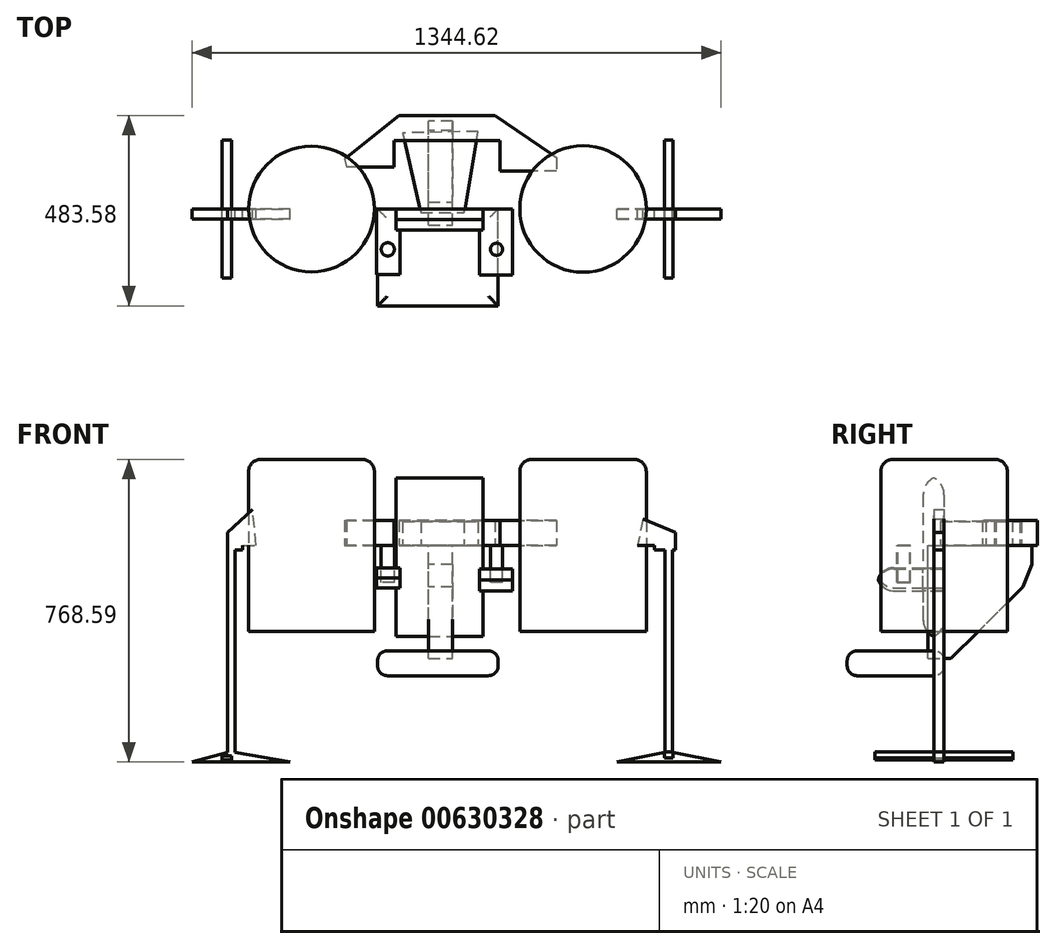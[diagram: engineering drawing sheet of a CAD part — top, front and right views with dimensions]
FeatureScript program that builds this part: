
annotation { "Feature Type Name" : "Feature", "Feature Type Description" : "" }
export const myFeature = defineFeature(function(context is Context, id is Id, definition is map)
    precondition{}
    {
        {
            var Q0;
            Q0=qCreatedBy(makeId("Top.planeOp"),FACE);
            var sketch = newSketch(context, id + "F0", { "sketchPlane" : qUnion([Q0])});
            skCircle(sketch, "E0", {"center": v(167.62, 0) * mm, "radius": 160.63 * mm});
            skCircle(sketch, "E1", {"center": v(-522.28, 0) * mm, "radius": 159.73 * mm});
            skSolve(sketch);
        }
        {
            var Q0;
            Q0 = qSketchRegion(id + "F0", true);
            extrude(context, id + "F1", {"entities" : qUnion([Q0]), "endBound" : BoundingType.SYMMETRIC, "depth" : 436.88 * mm, "offsetDistance" : 25.4 * mm});
        }
        {
            var Q0;
            Q0=qCreatedBy(makeId("Top.planeOp"),FACE);
            var sketch = newSketch(context, id + "F2", { "sketchPlane" : qUnion([Q0])});
            skLineSegment(sketch, "E2", {"start": v(-437.65, 127.2) * mm, "end": v(-300.14, 237.2) * mm});
            skLineSegment(sketch, "E3", {"start": v(-300.14, 237.2) * mm, "end": v(-56.56, 237.2) * mm});
            skLineSegment(sketch, "E4", {"start": v(-56.56, 237.2) * mm, "end": v(99.61, 131.12) * mm});
            skLineSegment(sketch, "E5", {"start": v(99.61, 131.12) * mm, "end": v(99.61, 96.75) * mm});
            skLineSegment(sketch, "E6", {"start": v(99.61, 96.75) * mm, "end": v(-42.8, 96.75) * mm});
            skLineSegment(sketch, "E7", {"start": v(-42.8, 96.75) * mm, "end": v(-42.8, 173.36) * mm});
            skLineSegment(sketch, "E8", {"start": v(-42.8, 173.36) * mm, "end": v(-312.04, 173.36) * mm});
            skLineSegment(sketch, "E9", {"start": v(-312.04, 173.36) * mm, "end": v(-312.04, 106.57) * mm});
            skLineSegment(sketch, "E10", {"start": v(-312.04, 106.57) * mm, "end": v(-432.74, 106.57) * mm});
            skLineSegment(sketch, "E11", {"start": v(-437.65, 127.2) * mm, "end": v(-432.74, 106.57) * mm});
            skSolve(sketch);
        }
        {
            var Q0;
            Q0 = qSketchRegion(id + "F2", true);
            extrude(context, id + "F3", {"entities" : qUnion([Q0]), "depth" : 63.5 * mm, "offsetDistance" : 25.4 * mm});
        }
        {
            var Q0;
            Q0=qCreatedBy(makeId("Front.planeOp"),FACE);
            var sketch = newSketch(context, id + "F4", { "sketchPlane" : qUnion([Q0])});
            skLineSegment(sketch, "E12.bottom", {"start": v(-86.02, 177.29) * mm, "end": v(-308, 177.29) * mm});
            skLineSegment(sketch, "E12.top", {"start": v(-86.02, -237.2) * mm, "end": v(-308, -237.2) * mm});
            skLineSegment(sketch, "E12.left", {"start": v(-86.02, 177.29) * mm, "end": v(-86.02, -237.2) * mm});
            skLineSegment(sketch, "E12.right", {"start": v(-308, 177.29) * mm, "end": v(-308, -237.2) * mm});
            skPoint(sketch, "E12.middle", {"position": v(-197.01, -29.96) * mm});
            skLineSegment(sketch, "E13.bottom", {"start": v(-47.84, -268.15) * mm, "end": v(-354.28, -268.15) * mm});
            skLineSegment(sketch, "E13.top", {"start": v(-47.84, -331) * mm, "end": v(-354.28, -331) * mm});
            skLineSegment(sketch, "E13.left", {"start": v(-47.84, -268.15) * mm, "end": v(-47.84, -331) * mm});
            skLineSegment(sketch, "E13.right", {"start": v(-354.28, -268.15) * mm, "end": v(-354.28, -331) * mm});
            skPoint(sketch, "E13.middle", {"position": v(-201.06, -299.58) * mm});
            skSolve(sketch);
        }
        {
            var Q0;
            Q0=makeQuery(id+"F4.imprint","IMPRINT",FACE,{"disambiguationData":[TD([[makeQuery(id+"F4.imprint","IMPRINT",EDGE,{"derivedFrom":sQuery(id+"F4.wireOp",EDGE,"E12.bottom")}),1.0]])]});
            extrude(context, id + "F5", {"entities" : qUnion([Q0]), "depth" : 53.34 * mm, "offsetDistance" : 25.4 * mm});
        }
        {
            var Q0;
            Q0=makeQuery(id+"F5.opExtrude","CAP_EDGE",EDGE,{"disambiguationData":[OSD([sQuery(id+"F4.wireOp",EDGE,"E12.top")])],"isStart":true});
            var Q1;
            Q1=makeQuery(id+"F5.opExtrude","CAP_EDGE",EDGE,{"disambiguationData":[OSD([sQuery(id+"F4.wireOp",EDGE,"E12.top")])],"isStart":false});
            var Q2;
            Q2=makeQuery(id+"F5.opExtrude","CAP_EDGE",EDGE,{"disambiguationData":[OSD([sQuery(id+"F4.wireOp",EDGE,"E12.bottom")])],"isStart":false});
            var Q3;
            Q3=makeQuery(id+"F5.opExtrude","CAP_EDGE",EDGE,{"disambiguationData":[OSD([sQuery(id+"F4.wireOp",EDGE,"E12.bottom")])],"isStart":true});
            fillet(context, id + "F6", {"entities" : qUnion([Q0, Q1, Q2, Q3]), "radius" : 49.06 * mm, "tangentPropagation" : true, "allowEdgeOverflow" : false});
        }
        {
            var Q0;
            Q0=qCreatedBy(makeId("Top.planeOp"),FACE);
            var sketch = newSketch(context, id + "F7", { "sketchPlane" : qUnion([Q0])});
            skLineSegment(sketch, "E14", {"start": v(-290.32, 192.98) * mm, "end": v(-244.16, -9.35) * mm});
            skLineSegment(sketch, "E15", {"start": v(-244.16, -9.35) * mm, "end": v(-134.15, -9.35) * mm});
            skLineSegment(sketch, "E16", {"start": v(-134.15, -9.35) * mm, "end": v(-98.8, 196.91) * mm});
            skLineSegment(sketch, "E17", {"start": v(-98.8, 196.91) * mm, "end": v(-290.32, 192.98) * mm});
            skSolve(sketch);
        }
        {
            var Q0;
            Q0 = qSketchRegion(id + "F7", true);
            extrude(context, id + "F8", {"entities" : qUnion([Q0]), "depth" : 60.96 * mm, "offsetDistance" : 25.4 * mm});
        }
        {
            var Q0;
            Q0=makeQuery(id+"F4.imprint","IMPRINT",FACE,{"disambiguationData":[TD([[makeQuery(id+"F4.imprint","IMPRINT",EDGE,{"derivedFrom":sQuery(id+"F4.wireOp",EDGE,"E13.bottom")}),1.0]])]});
            extrude(context, id + "F9", {"entities" : qUnion([Q0]), "depth" : 246.38 * mm, "offsetDistance" : 25.4 * mm});
        }
        {
            var Q0;
            Q0=makeQuery(id+"F9.opExtrude","SWEPT_EDGE",EDGE,{"disambiguationData":[OSD([sQuery(id+"F4.wireOp",EDGE,"E13.bottom"),sQuery(id+"F4.wireOp",EDGE,"E13.right")])]});
            var Q1;
            Q1=makeQuery(id+"F9.opExtrude","SWEPT_EDGE",EDGE,{"disambiguationData":[OSD([sQuery(id+"F4.wireOp",EDGE,"E13.top"),sQuery(id+"F4.wireOp",EDGE,"E13.right")])]});
            var Q2;
            Q2=makeQuery(id+"F9.opExtrude","SWEPT_EDGE",EDGE,{"disambiguationData":[OSD([sQuery(id+"F4.wireOp",EDGE,"E13.bottom"),sQuery(id+"F4.wireOp",EDGE,"E13.left")])]});
            var Q3;
            Q3=makeQuery(id+"F9.opExtrude","SWEPT_EDGE",EDGE,{"disambiguationData":[OSD([sQuery(id+"F4.wireOp",EDGE,"E13.top"),sQuery(id+"F4.wireOp",EDGE,"E13.left")])]});
            var Q4;
            Q4=makeQuery(id+"F9.opExtrude","CAP_EDGE",EDGE,{"disambiguationData":[OSD([sQuery(id+"F4.wireOp",EDGE,"E13.bottom")])],"isStart":false});
            var Q5;
            Q5=makeQuery(id+"F9.opExtrude","CAP_EDGE",EDGE,{"disambiguationData":[OSD([sQuery(id+"F4.wireOp",EDGE,"E13.top")])],"isStart":false});
            var Q6;
            Q6=makeQuery(id+"F9.opExtrude","CAP_EDGE",EDGE,{"disambiguationData":[OSD([sQuery(id+"F4.wireOp",EDGE,"E13.bottom")])],"isStart":true});
            var Q7;
            Q7=makeQuery(id+"F9.opExtrude","CAP_EDGE",EDGE,{"disambiguationData":[OSD([sQuery(id+"F4.wireOp",EDGE,"E13.top")])],"isStart":true});
            fillet(context, id + "F10", {"entities" : qUnion([Q0, Q1, Q2, Q3, Q4, Q5, Q6, Q7]), "radius" : 24.53 * mm, "tangentPropagation" : true, "allowEdgeOverflow" : false});
        }
        {
            var Q0;
            Q0=qCreatedBy(makeId("Top.planeOp"),FACE);
            var sketch = newSketch(context, id + "F11", { "sketchPlane" : qUnion([Q0])});
            skLineSegment(sketch, "E18.bottom", {"start": v(-225.08, -41.15) * mm, "end": v(-163.53, -41.15) * mm});
            skLineSegment(sketch, "E18.top", {"start": v(-225.08, 223.45) * mm, "end": v(-163.53, 223.45) * mm});
            skLineSegment(sketch, "E18.left", {"start": v(-225.08, -41.15) * mm, "end": v(-225.08, 223.45) * mm});
            skLineSegment(sketch, "E18.right", {"start": v(-163.53, -41.15) * mm, "end": v(-163.53, 223.45) * mm});
            skSolve(sketch);
        }
        {
            var Q0;
            Q0 = qSketchRegion(id + "F11", true);
            extrude(context, id + "F12", {"entities" : qUnion([Q0]), "oppositeDirection" : true, "depth" : 287.78 * mm, "offsetDistance" : 25.4 * mm});
        }
        {
            var Q0;
            Q0=makeQuery(id+"F12.opExtrude","CAP_EDGE",EDGE,{"disambiguationData":[OSD([sQuery(id+"F11.wireOp",EDGE,"E18.top")])],"isStart":false});
            chamfer(context, id + "F13", {"entities" : qUnion([Q0]), "width" : 205.74 * mm, "tangentPropagation" : true});
        }
        {
            var Q0;
            {var subQ0=sQuery(id+"F11.wireOp",EDGE,"E18.top");Q0=makeQuery(id+"F13.opChamfer","BLEND_EDGE",EDGE,{"blendedFrom":[makeQuery(id+"F12.opExtrude","CAP_EDGE",EDGE,{"disambiguationData":[OSD([subQ0])],"isStart":false}),makeQuery(id+"F12.opExtrude","SWEPT_FACE",FACE,{"disambiguationData":[OSD([subQ0])]})],"blendedInto":[makeQuery(id+"F12.opExtrude","SWEPT_FACE",FACE,{"disambiguationData":[OSD([subQ0])]})]});}
            chamfer(context, id + "F14", {"entities" : qUnion([Q0]), "width" : 81.28 * mm, "tangentPropagation" : true});
        }
        {
            var Q0;
            Q0=qCreatedBy(makeId("Top.planeOp"),FACE);
            var sketch = newSketch(context, id + "F15", { "sketchPlane" : qUnion([Q0])});
            skCircle(sketch, "E19", {"center": v(-525.07, 0) * mm, "radius": 114.29 * mm});
            skCircle(sketch, "E20", {"center": v(169.35, 0) * mm, "radius": 110.47 * mm});
            skSolve(sketch);
        }
        {
            var Q0;
            Q0=sQuery(id+"F15.wireOp",EDGE,"E19");
            var Q1;
            Q1=sQuery(id+"F15.wireOp",EDGE,"E20");
            extrude(context, id + "F16", {"bodyType" : ToolBodyType.SURFACE, "surfaceEntities" : qUnion([Q0, Q1]), "oppositeDirection" : true, "depth" : 365.76 * mm, "offsetDistance" : 25.4 * mm});
        }
        {
            var Q0;
            Q0=qCreatedBy(makeId("Top.planeOp"),FACE);
            var sketch = newSketch(context, id + "F17", { "sketchPlane" : qUnion([Q0])});
            skCircle(sketch, "E21", {"center": v(-529, 0) * mm, "radius": 62.35 * mm});
            skCircle(sketch, "E22", {"center": v(171.31, 0) * mm, "radius": 55.52 * mm});
            skSolve(sketch);
        }
        {
            var Q0;
            Q0=sQuery(id+"F17.wireOp",EDGE,"E21");
            var Q1;
            Q1=sQuery(id+"F17.wireOp",EDGE,"E22");
            extrude(context, id + "F18", {"bodyType" : ToolBodyType.SURFACE, "surfaceEntities" : qUnion([Q0, Q1]), "oppositeDirection" : true, "depth" : 414.02 * mm, "offsetDistance" : 25.4 * mm});
        }
        {
            var Q0;
            Q0=qCreatedBy(makeId("Front.planeOp"),FACE);
            var sketch = newSketch(context, id + "F19", { "sketchPlane" : qUnion([Q0])});
            skLineSegment(sketch, "E23", {"start": v(-672.3, 90.77) * mm, "end": v(-735.08, 32.96) * mm});
            skLineSegment(sketch, "E24", {"start": v(-735.08, 32.96) * mm, "end": v(-735.08, -11.64) * mm});
            skLineSegment(sketch, "E25", {"start": v(-735.08, -11.64) * mm, "end": v(-697.09, -11.64) * mm});
            skLineSegment(sketch, "E26", {"start": v(-697.09, -11.64) * mm, "end": v(-697.09, 0) * mm});
            skLineSegment(sketch, "E27", {"start": v(-697.09, 0) * mm, "end": v(-662.4, 0) * mm});
            skLineSegment(sketch, "E28", {"start": v(-662.4, 0) * mm, "end": v(-672.3, 90.77) * mm});
            skLineSegment(sketch, "E29", {"start": v(320.46, 67.65) * mm, "end": v(305.6, 0) * mm});
            skLineSegment(sketch, "E30", {"start": v(305.6, 0) * mm, "end": v(348.54, 0) * mm});
            skLineSegment(sketch, "E31", {"start": v(348.54, 0) * mm, "end": v(348.54, -11.64) * mm});
            skLineSegment(sketch, "E32", {"start": v(348.54, -11.64) * mm, "end": v(403.05, -11.64) * mm});
            skLineSegment(sketch, "E33", {"start": v(403.05, -11.64) * mm, "end": v(403.05, 32.96) * mm});
            skLineSegment(sketch, "E34", {"start": v(403.05, 32.96) * mm, "end": v(320.46, 67.65) * mm});
            skLineSegment(sketch, "E35.bottom", {"start": v(375.8, -11.64) * mm, "end": v(394.8, -11.64) * mm});
            skLineSegment(sketch, "E35.top", {"start": v(375.8, -525.37) * mm, "end": v(394.8, -525.37) * mm});
            skLineSegment(sketch, "E35.left", {"start": v(375.8, -11.64) * mm, "end": v(375.8, -525.37) * mm});
            skLineSegment(sketch, "E35.right", {"start": v(394.8, -11.64) * mm, "end": v(394.8, -525.37) * mm});
            skLineSegment(sketch, "E36.bottom", {"start": v(-716.08, -11.64) * mm, "end": v(-735.08, -11.64) * mm});
            skLineSegment(sketch, "E36.top", {"start": v(-716.08, -525.37) * mm, "end": v(-735.08, -525.37) * mm});
            skLineSegment(sketch, "E36.left", {"start": v(-716.08, -11.64) * mm, "end": v(-716.08, -525.37) * mm});
            skLineSegment(sketch, "E36.right", {"start": v(-735.08, -11.64) * mm, "end": v(-735.08, -525.37) * mm});
            skLineSegment(sketch, "E37", {"start": v(-716.08, -525.37) * mm, "end": v(-576.5, -550.15) * mm});
            skLineSegment(sketch, "E38", {"start": v(-576.5, -550.15) * mm, "end": v(-825.93, -550.15) * mm});
            skLineSegment(sketch, "E39", {"start": v(-735.08, -525.37) * mm, "end": v(-825.93, -550.15) * mm});
            skLineSegment(sketch, "E40", {"start": v(375.8, -525.37) * mm, "end": v(254.39, -550.15) * mm});
            skLineSegment(sketch, "E41", {"start": v(254.39, -550.15) * mm, "end": v(518.69, -550.15) * mm});
            skLineSegment(sketch, "E42", {"start": v(518.69, -550.15) * mm, "end": v(394.8, -525.37) * mm});
            skSolve(sketch);
        }
        {
            var Q0;
            Q0 = qSketchRegion(id + "F19", true);
            extrude(context, id + "F20", {"entities" : qUnion([Q0]), "depth" : 25.4 * mm, "offsetDistance" : 25.4 * mm});
        }
        {
            var Q0;
            Q0=qCreatedBy(makeId("Front.planeOp"),FACE);
            var sketch = newSketch(context, id + "F21", { "sketchPlane" : qUnion([Q0])});
            skLineSegment(sketch, "E43.bottom", {"start": v(-725.78, -534.26) * mm, "end": v(-748.75, -534.26) * mm});
            skLineSegment(sketch, "E43.top", {"start": v(-725.78, -544.98) * mm, "end": v(-748.75, -544.98) * mm});
            skLineSegment(sketch, "E43.left", {"start": v(-725.78, -534.26) * mm, "end": v(-725.78, -544.98) * mm});
            skLineSegment(sketch, "E43.right", {"start": v(-748.75, -534.26) * mm, "end": v(-748.75, -544.98) * mm});
            skLineSegment(sketch, "E44.bottom", {"start": v(396.57, -540.39) * mm, "end": v(375.13, -540.39) * mm});
            skLineSegment(sketch, "E44.top", {"start": v(396.57, -525.08) * mm, "end": v(375.13, -525.08) * mm});
            skLineSegment(sketch, "E44.left", {"start": v(396.57, -540.39) * mm, "end": v(396.57, -525.08) * mm});
            skLineSegment(sketch, "E44.right", {"start": v(375.13, -540.39) * mm, "end": v(375.13, -525.08) * mm});
            skSolve(sketch);
        }
        {
            var Q0;
            Q0 = qSketchRegion(id + "F21", true);
            extrude(context, id + "F22", {"entities" : qUnion([Q0]), "endBound" : BoundingType.SYMMETRIC, "depth" : 350.52 * mm, "offsetDistance" : 25.4 * mm});
        }
        {
            var Q0;
            Q0=qCreatedBy(makeId("Front.planeOp"),FACE);
            var sketch = newSketch(context, id + "F23", { "sketchPlane" : qUnion([Q0])});
            skLineSegment(sketch, "E45.bottom", {"start": v(-95.45, -59.31) * mm, "end": v(-11.79, -59.31) * mm});
            skLineSegment(sketch, "E45.top", {"start": v(-95.45, -115.53) * mm, "end": v(-11.79, -115.53) * mm});
            skLineSegment(sketch, "E45.left", {"start": v(-95.45, -59.31) * mm, "end": v(-95.45, -115.53) * mm});
            skLineSegment(sketch, "E45.right", {"start": v(-11.79, -59.31) * mm, "end": v(-11.79, -115.53) * mm});
            skLineSegment(sketch, "E46.bottom", {"start": v(-296.77, -56.7) * mm, "end": v(-356.9, -56.7) * mm});
            skLineSegment(sketch, "E46.top", {"start": v(-296.77, -107.68) * mm, "end": v(-356.9, -107.68) * mm});
            skLineSegment(sketch, "E46.left", {"start": v(-296.77, -56.7) * mm, "end": v(-296.77, -107.68) * mm});
            skLineSegment(sketch, "E46.right", {"start": v(-356.9, -56.7) * mm, "end": v(-356.9, -107.68) * mm});
            skSolve(sketch);
        }
        {
            var Q0;
            Q0 = qSketchRegion(id + "F23", true);
            extrude(context, id + "F24", {"entities" : qUnion([Q0]), "operationType" : NewBodyOperationType.ADD, "depth" : 170.18 * mm, "offsetDistance" : 25.4 * mm});
        }
        {
            var Q0;
            Q0=makeQuery(id+"F24.opExtrude","CAP_EDGE",EDGE,{"disambiguationData":[OSD([sQuery(id+"F23.wireOp",EDGE,"E46.bottom")])],"isStart":false});
            var Q1;
            Q1=makeQuery(id+"F24.opExtrude","CAP_EDGE",EDGE,{"disambiguationData":[OSD([sQuery(id+"F23.wireOp",EDGE,"E45.bottom")])],"isStart":false});
            var Q2;
            Q2=makeQuery(id+"F24.opExtrude","CAP_EDGE",EDGE,{"disambiguationData":[OSD([sQuery(id+"F23.wireOp",EDGE,"E45.top")])],"isStart":false});
            var Q3;
            Q3=makeQuery(id+"F24.opExtrude","CAP_EDGE",EDGE,{"disambiguationData":[OSD([sQuery(id+"F23.wireOp",EDGE,"E46.top")])],"isStart":false});
            fillet(context, id + "F25", {"entities" : qUnion([Q0, Q1, Q2, Q3]), "radius" : 42.92 * mm, "tangentPropagation" : true, "allowEdgeOverflow" : false});
        }
        {
            var Q0;
            Q0=makeQuery(id+"F1.opExtrude","CAP_EDGE",EDGE,{"disambiguationData":[OSD([sQuery(id+"F0.wireOp",EDGE,"E0")])],"isStart":false});
            var Q1;
            Q1=makeQuery(id+"F1.opExtrude","CAP_FACE",FACE,{"disambiguationData":[OSD([sQuery(id+"F0.wireOp",EDGE,"E0")])],"isStart":false});
            var Q2;
            Q2=makeQuery(id+"F1.opExtrude","CAP_EDGE",EDGE,{"disambiguationData":[OSD([sQuery(id+"F0.wireOp",EDGE,"E1")])],"isStart":false});
            fillet(context, id + "F26", {"entities" : qUnion([Q0, Q1, Q2]), "radius" : 30.66 * mm, "tangentPropagation" : true, "allowEdgeOverflow" : false});
        }
        {
            var Q0;
            Q0=qCreatedBy(makeId("Top.planeOp"),FACE);
            var sketch = newSketch(context, id + "F27", { "sketchPlane" : qUnion([Q0])});
            skCircle(sketch, "E47", {"center": v(-328.31, -102.63) * mm, "radius": 16.78 * mm});
            skCircle(sketch, "E48", {"center": v(-52.15, -102.46) * mm, "radius": 15.46 * mm});
            skSolve(sketch);
        }
        {
            var Q0;
            Q0 = qSketchRegion(id + "F27", true);
            extrude(context, id + "F28", {"entities" : qUnion([Q0]), "oppositeDirection" : true, "depth" : 93.72 * mm, "offsetDistance" : 25.4 * mm});
        }
    });
